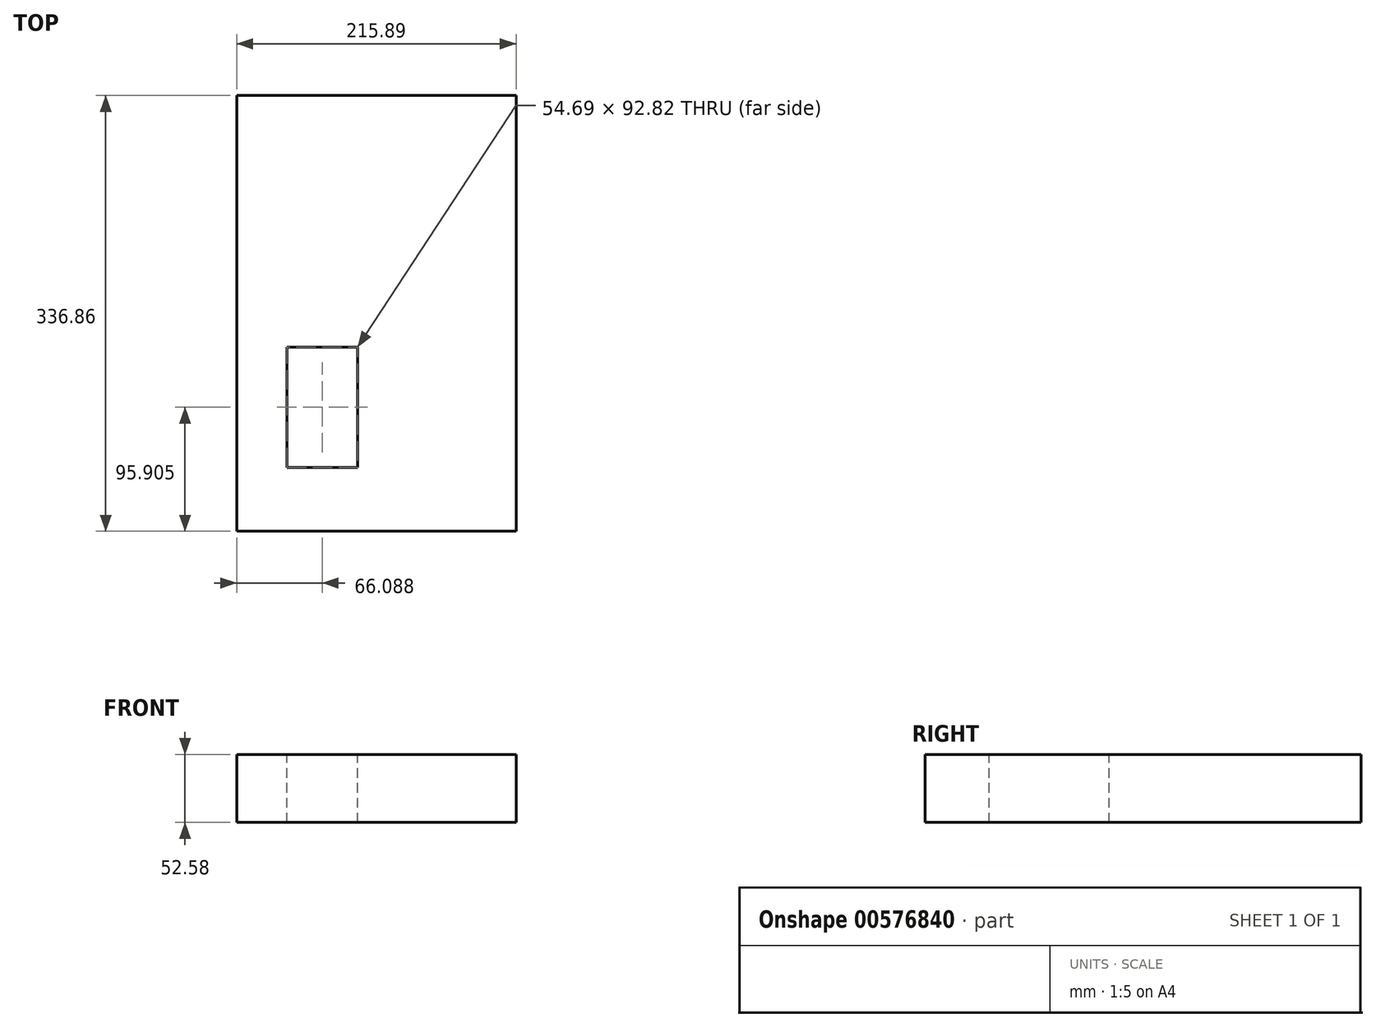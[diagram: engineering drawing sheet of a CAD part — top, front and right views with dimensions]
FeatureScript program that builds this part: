
annotation { "Feature Type Name" : "Feature", "Feature Type Description" : "" }
export const myFeature = defineFeature(function(context is Context, id is Id, definition is map)
    precondition{}
    {
        {
            var Q0;
            Q0=qCreatedBy(makeId("Top.planeOp"),FACE);
            var sketch = newSketch(context, id + "F0", { "sketchPlane" : qUnion([Q0])});
            skLineSegment(sketch, "E0.bottom", {"start": v(0, 0) * mm, "end": v(215.89, 0) * mm});
            skLineSegment(sketch, "E0.top", {"start": v(0, 336.86) * mm, "end": v(215.89, 336.86) * mm});
            skLineSegment(sketch, "E0.left", {"start": v(0, 0) * mm, "end": v(0, 336.86) * mm});
            skLineSegment(sketch, "E0.right", {"start": v(215.89, 0) * mm, "end": v(215.89, 336.86) * mm});
            skSolve(sketch);
        }
        {
            var Q0;
            Q0 = qSketchRegion(id + "F0", true);
            extrude(context, id + "F1", {"entities" : qUnion([Q0]), "depth" : 52.58 * mm, "offsetDistance" : 25.4 * mm});
        }
        {
            var Q0;
            Q0=makeQuery(id+"F1.opExtrude","CAP_FACE",FACE,{"disambiguationData":[OSD([sQuery(id+"F0.wireOp",EDGE,"E0.bottom"),sQuery(id+"F0.wireOp",EDGE,"E0.top"),sQuery(id+"F0.wireOp",EDGE,"E0.left"),sQuery(id+"F0.wireOp",EDGE,"E0.right")])],"isStart":false});
            var sketch = newSketch(context, id + "F2", { "sketchPlane" : qUnion([Q0])});
            skLineSegment(sketch, "E1", {"start": v(38.74, 49.5) * mm, "end": v(38.74, 142.32) * mm});
            skLineSegment(sketch, "E2", {"start": v(38.74, 142.32) * mm, "end": v(93.43, 142.32) * mm});
            skLineSegment(sketch, "E3", {"start": v(93.43, 142.32) * mm, "end": v(93.43, 49.5) * mm});
            skLineSegment(sketch, "E4", {"start": v(93.43, 49.5) * mm, "end": v(38.74, 49.5) * mm});
            skSolve(sketch);
        }
        {
            var Q0;
            Q0 = qSketchRegion(id + "F2", true);
            extrude(context, id + "F3", {"entities" : qUnion([Q0]), "operationType" : NewBodyOperationType.REMOVE, "endBound" : BoundingType.THROUGH_ALL, "oppositeDirection" : true, "depth" : 137.4 * mm, "offsetDistance" : 25.4 * mm});
        }
    });
